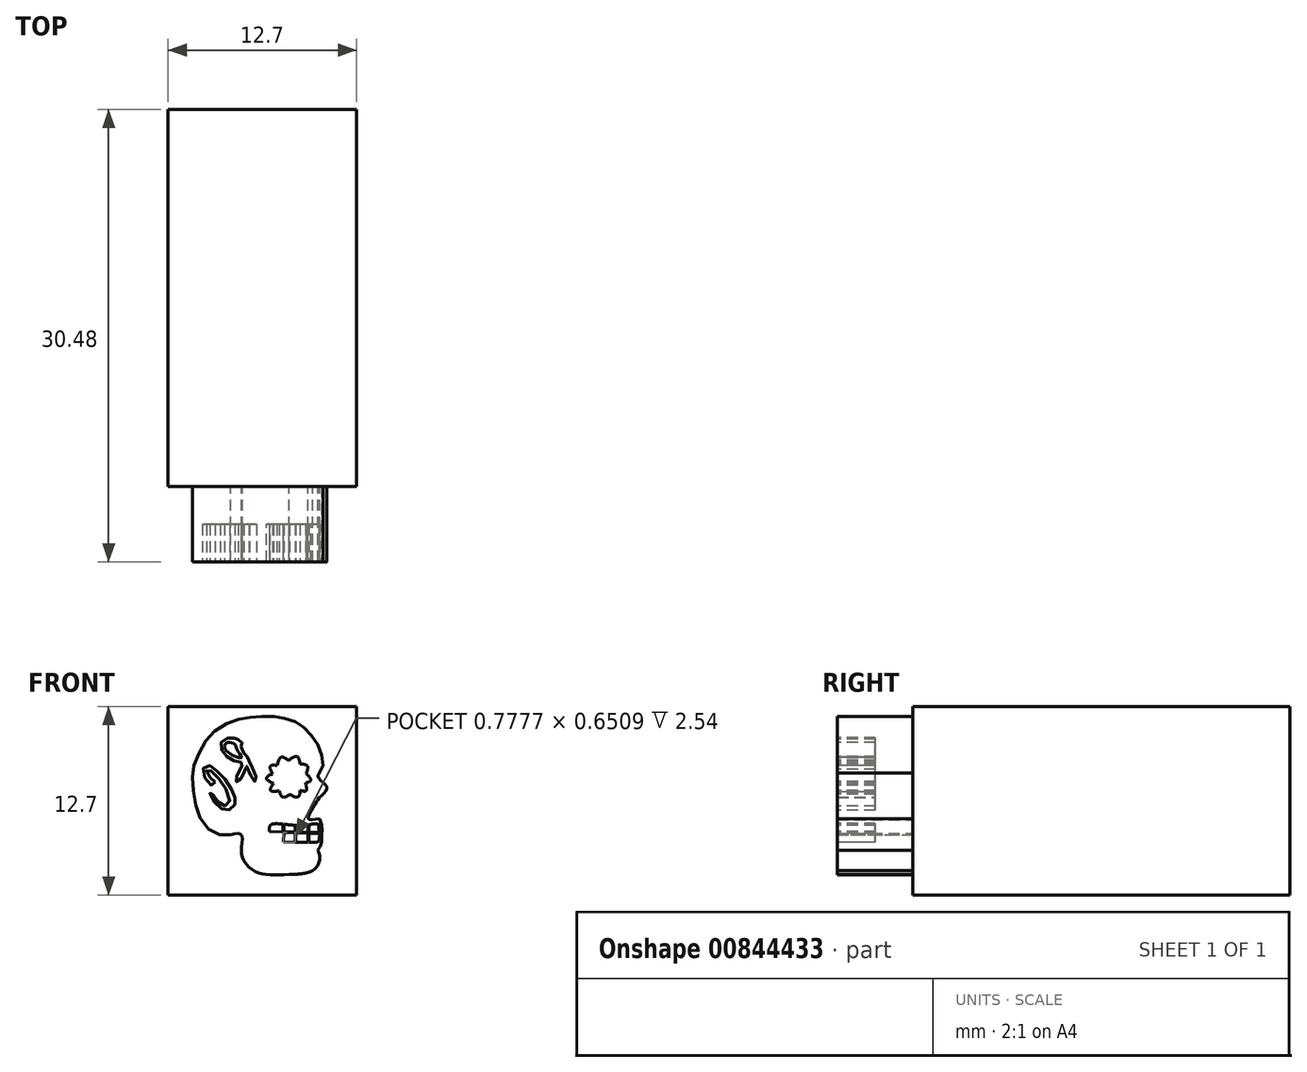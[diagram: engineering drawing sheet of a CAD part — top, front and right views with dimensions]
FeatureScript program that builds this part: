
annotation { "Feature Type Name" : "Feature", "Feature Type Description" : "" }
export const myFeature = defineFeature(function(context is Context, id is Id, definition is map)
    precondition{}
    {
        {
            var Q0;
            Q0=qCreatedBy(makeId("Front.planeOp"),FACE);
            var sketch = newSketch(context, id + "F0", { "sketchPlane" : qUnion([Q0])});
            skArc(sketch, "E0", {"start": v(-2.96, 1.65) * mm, "mid": v(-2.52, 2.28) * mm, "end": v(-2.62, 3.03) * mm});
            skFitSpline(sketch, "E1", {"points": [v(-4.55, 1.4) * mm, v(-2.96, 1.65) * mm], "startDerivative": vector(1.7, 0) * mm, "endDerivative": vector(1.51, 0.7) * mm});
            skFitSpline(sketch, "E2", {"points": [v(-2.49, 5.13) * mm, v(-2.35, 4.58) * mm, v(-2.35, 4.15) * mm, v(-2.35, 3.77) * mm, v(-2.62, 3.03) * mm], "startDerivative": vector(1.13, -2.5) * mm, "endDerivative": vector(-2.25, -2.73) * mm});
            skFitSpline(sketch, "E3", {"points": [v(-8.49, 4.08) * mm, v(-9.32, 4.08) * mm, v(-10.36, 4.88) * mm, v(-10.86, 6.14) * mm, v(-11.05, 7.58) * mm, v(-10.98, 8.64) * mm, v(-10.5, 9.83) * mm, v(-9.7, 10.94) * mm, v(-8.49, 11.66) * mm, v(-7.5, 11.93) * mm, v(-6.53, 12.03) * mm, v(-5.49, 12.02) * mm, v(-4.7, 11.87) * mm, v(-3.86, 11.55) * mm, v(-3.27, 11.01) * mm, v(-2.68, 10.28) * mm, v(-2.36, 9.45) * mm, v(-2.28, 8.68) * mm, v(-2.5, 8.22) * mm], "startDerivative": vector(-16.18, -2.66) * mm, "endDerivative": vector(-3.8, -12.82) * mm});
            skFitSpline(sketch, "E4", {"points": [v(-2.49, 5.13) * mm, v(-3.25, 5.13) * mm, v(-2.88, 5.99) * mm, v(-2.49, 6.59) * mm, v(-2, 7.19) * mm, v(-2.35, 7.65) * mm, v(-2.5, 8.22) * mm], "startDerivative": vector(-6.38, 0.02) * mm, "endDerivative": vector(4.2, 4.48) * mm});
            skFitSpline(sketch, "E5", {"points": [v(-8.49, 4.08) * mm, v(-7.77, 4.08) * mm, v(-7.74, 3.33) * mm, v(-7.65, 2.44) * mm, v(-6.94, 1.64) * mm, v(-6.06, 1.39) * mm, v(-4.55, 1.4) * mm], "startDerivative": vector(6.23, 1.32) * mm, "endDerivative": vector(7.7, 0.3) * mm});
            skSolve(sketch);
        }
        {
            var Q0;
            Q0=qCreatedBy(makeId("Front.planeOp"),FACE);
            var sketch = newSketch(context, id + "F1", { "sketchPlane" : qUnion([Q0])});
            skLineSegment(sketch, "E6.bottom", {"start": v(0, 0) * mm, "end": v(-12.7, 0) * mm});
            skLineSegment(sketch, "E6.top", {"start": v(0, 12.7) * mm, "end": v(-12.7, 12.7) * mm});
            skLineSegment(sketch, "E6.left", {"start": v(0, 0) * mm, "end": v(0, 12.7) * mm});
            skLineSegment(sketch, "E6.right", {"start": v(-12.7, 0) * mm, "end": v(-12.7, 12.7) * mm});
            skSolve(sketch);
        }
        {
            var Q0;
            Q0=qSketchRegion(id+"F0",true);
            extrude(context, id + "F2", {"entities" : qUnion([Q0]), "depth" : 5.08 * mm, "offsetDistance" : 25.4 * mm});
        }
        {
            var Q0;
            Q0=makeQuery(id+"F2.opExtrude","CAP_FACE",FACE,{"disambiguationData":[OSD([sQuery(id+"F0.wireOp",EDGE,"E0"),sQuery(id+"F0.wireOp",EDGE,"E1"),sQuery(id+"F0.wireOp",EDGE,"E2"),sQuery(id+"F0.wireOp",EDGE,"E3"),sQuery(id+"F0.wireOp",EDGE,"E4"),sQuery(id+"F0.wireOp",EDGE,"E5")])],"isStart":false});
            var sketch = newSketch(context, id + "F3", { "sketchPlane" : qUnion([Q0])});
            skFitSpline(sketch, "E7", {"points": [v(-5.37, 8.72) * mm, v(-5.09, 9.3) * mm, v(-4.59, 9.09) * mm], "startDerivative": vector(0.47, 1.45) * mm, "endDerivative": vector(1.15, -0.78) * mm});
            skFitSpline(sketch, "E8", {"points": [v(-4.59, 9.09) * mm, v(-4, 9.34) * mm, v(-3.8, 8.84) * mm], "startDerivative": vector(1.32, 0.85) * mm, "endDerivative": vector(0.23, -1.41) * mm});
            skFitSpline(sketch, "E9", {"points": [v(-3.8, 8.84) * mm, v(-3.33, 8.7) * mm, v(-3.4, 8.2) * mm], "startDerivative": vector(1.47, -0.06) * mm, "endDerivative": vector(-0.68, -1.2) * mm});
            skFitSpline(sketch, "E10", {"points": [v(-3.4, 8.2) * mm, v(-3.09, 7.74) * mm, v(-3.45, 7.56) * mm], "startDerivative": vector(0.96, -0.98) * mm, "endDerivative": vector(-1.07, -0.3) * mm});
            skFitSpline(sketch, "E11", {"points": [v(-3.45, 7.56) * mm, v(-3.4, 7.03) * mm, v(-3.8, 7.05) * mm], "startDerivative": vector(0.3, -1.24) * mm, "endDerivative": vector(-1.07, 0.2) * mm});
            skFitSpline(sketch, "E12", {"points": [v(-3.8, 7.05) * mm, v(-3.96, 6.61) * mm, v(-4.5, 6.8) * mm], "startDerivative": vector(-0.06, -1.45) * mm, "endDerivative": vector(-1.31, 0.89) * mm});
            skFitSpline(sketch, "E13", {"points": [v(-4.5, 6.8) * mm, v(-4.97, 6.6) * mm, v(-5.2, 7.02) * mm], "startDerivative": vector(-1.11, -0.95) * mm, "endDerivative": vector(-0.36, 1.4) * mm});
            skFitSpline(sketch, "E14", {"points": [v(-5.2, 7.02) * mm, v(-5.8, 7.05) * mm, v(-5.6, 7.52) * mm], "startDerivative": vector(-1.8, -0.17) * mm, "endDerivative": vector(1.04, 1.25) * mm});
            skFitSpline(sketch, "E15", {"points": [v(-5.6, 7.52) * mm, v(-6.08, 7.87) * mm, v(-5.65, 8.17) * mm], "startDerivative": vector(-1.95, 0.8) * mm, "endDerivative": vector(1.88, 0.54) * mm});
            skFitSpline(sketch, "E16", {"points": [v(-5.65, 8.17) * mm, v(-5.82, 8.67) * mm, v(-5.37, 8.72) * mm], "startDerivative": vector(-1.13, 1.61) * mm, "endDerivative": vector(1.77, -0.5) * mm});
            skFitSpline(sketch, "E17", {"points": [v(-2.58, 4.77) * mm, v(-3.23, 4.74) * mm, v(-4.58, 4.74) * mm, v(-5.8, 4.73) * mm, v(-5.9, 4.23) * mm, v(-5.82, 3.73) * mm, v(-5, 3.58) * mm, v(-3.89, 3.56) * mm, v(-2.84, 3.54) * mm, v(-2.58, 3.63) * mm, v(-2.5, 4.16) * mm, v(-2.54, 4.47) * mm, v(-2.58, 4.77) * mm]});
            skLineSegment(sketch, "E18", {"start": v(-5.9, 4.28) * mm, "end": v(-2.51, 4.22) * mm});
            skLineSegment(sketch, "E19", {"start": v(-5.9, 4.23) * mm, "end": v(-2.5, 4.16) * mm});
            skLineSegment(sketch, "E20", {"start": v(-4.96, 4.78) * mm, "end": v(-4.99, 3.58) * mm});
            skLineSegment(sketch, "E21", {"start": v(-4.99, 3.58) * mm, "end": v(-5, 3.58) * mm});
            skLineSegment(sketch, "E22", {"start": v(-4.9, 4.78) * mm, "end": v(-4.92, 3.58) * mm});
            skLineSegment(sketch, "E23", {"start": v(-4.15, 4.7) * mm, "end": v(-4.15, 3.56) * mm});
            skLineSegment(sketch, "E24", {"start": v(-3.23, 4.74) * mm, "end": v(-3.23, 3.55) * mm});
            skLineSegment(sketch, "E25", {"start": v(-3.28, 4.73) * mm, "end": v(-3.28, 3.55) * mm});
            skLineSegment(sketch, "E26", {"start": v(-4.11, 4.7) * mm, "end": v(-4.11, 3.56) * mm});
            skSolve(sketch);
        }
        {
            var Q0;
            Q0=makeQuery(id+"F3.imprint","IMPRINT",FACE,{"disambiguationData":[TD([[makeQuery(id+"F3.imprint","IMPRINT",EDGE,{"derivedFrom":sQuery(id+"F3.wireOp",EDGE,"E7")}),-1.0]])]});
            var Q1;
            {var subQ0=sQuery(id+"F3.wireOp",EDGE,"E18");var subQ1=sQuery(id+"F3.wireOp",EDGE,"E17");var subQ2=makeQuery(id+"F3.imprint","INTERSECT",VERTEX,{"disambiguationData":[OD(0.0)],"derivedFrom":[subQ1,subQ0]});Q1=makeQuery(id+"F3.imprint","IMPRINT",FACE,{"disambiguationData":[TD([[makeQuery(id+"F3.imprint","IMPRINT",EDGE,{"disambiguationData":[TD([[subQ2,1.0]])],"derivedFrom":subQ1}),1.0]])]});}
            var Q2;
            {var subQ0=sQuery(id+"F3.wireOp",EDGE,"E22");var subQ1=sQuery(id+"F3.wireOp",EDGE,"E17");var subQ2=makeQuery(id+"F3.imprint","INTERSECT",VERTEX,{"disambiguationData":[OD(0.0)],"derivedFrom":[subQ1,subQ0]});Q2=makeQuery(id+"F3.imprint","IMPRINT",FACE,{"disambiguationData":[TD([[makeQuery(id+"F3.imprint","IMPRINT",EDGE,{"disambiguationData":[TD([[subQ2,1.0]])],"derivedFrom":subQ1}),1.0]])]});}
            var Q3;
            {var subQ0=sQuery(id+"F3.wireOp",EDGE,"nEHl1WmI-M9KE-TG4T-uo55-SjTNBp4atS7q");var subQ1=sQuery(id+"F3.wireOp",EDGE,"E17");var subQ2=makeQuery(id+"F3.imprint","INTERSECT",VERTEX,{"derivedFrom":[subQ1,subQ0]});Q3=makeQuery(id+"F3.imprint","IMPRINT",FACE,{"disambiguationData":[TD([[makeQuery(id+"F3.imprint","IMPRINT",EDGE,{"disambiguationData":[TD([[subQ2,1.0]])],"derivedFrom":subQ1}),1.0]])]});}
            var Q4;
            {var subQ0=sQuery(id+"F3.wireOp",EDGE,"E18");var subQ1=sQuery(id+"F3.wireOp",EDGE,"E17");var subQ2=makeQuery(id+"F3.imprint","INTERSECT",VERTEX,{"disambiguationData":[OD(1.0)],"derivedFrom":[subQ1,subQ0]});Q4=makeQuery(id+"F3.imprint","IMPRINT",FACE,{"disambiguationData":[TD([[makeQuery(id+"F3.imprint","IMPRINT",EDGE,{"disambiguationData":[TD([[subQ2,-1.0]])],"derivedFrom":subQ1}),1.0]])]});}
            var Q5;
            {var subQ0=sQuery(id+"F3.wireOp",EDGE,"E19");var subQ1=sQuery(id+"F3.wireOp",EDGE,"E17");var subQ2=makeQuery(id+"F3.imprint","INTERSECT",VERTEX,{"disambiguationData":[OD(1.0)],"derivedFrom":[subQ1,subQ0]});Q5=makeQuery(id+"F3.imprint","IMPRINT",FACE,{"disambiguationData":[TD([[makeQuery(id+"F3.imprint","IMPRINT",EDGE,{"disambiguationData":[TD([[subQ2,1.0]])],"derivedFrom":subQ1}),1.0]])]});}
            var Q6;
            {var subQ1=sQuery(id+"F3.wireOp",EDGE,"E17");var subQ3=makeQuery(id+"F3.imprint","IMPRINT",VERTEX,{"derivedFrom":subQ1});Q6=makeQuery(id+"F3.imprint","IMPRINT",FACE,{"disambiguationData":[TD([[makeQuery(id+"F3.imprint","IMPRINT",EDGE,{"disambiguationData":[TD([[subQ3,1.0]])],"derivedFrom":subQ1}),1.0]])]});}
            var Q7;
            {var subQ0=sQuery(id+"F3.wireOp",EDGE,"E22");var subQ1=sQuery(id+"F3.wireOp",EDGE,"E17");var subQ2=makeQuery(id+"F3.imprint","INTERSECT",VERTEX,{"disambiguationData":[OD(1.0)],"derivedFrom":[subQ1,subQ0]});Q7=makeQuery(id+"F3.imprint","IMPRINT",FACE,{"disambiguationData":[TD([[makeQuery(id+"F3.imprint","IMPRINT",EDGE,{"disambiguationData":[TD([[subQ2,-1.0]])],"derivedFrom":subQ1}),1.0]])]});}
            var Q8;
            {var subQ0=sQuery(id+"F3.wireOp",EDGE,"E25");var subQ1=sQuery(id+"F3.wireOp",EDGE,"E17");var subQ2=makeQuery(id+"F3.imprint","INTERSECT",VERTEX,{"disambiguationData":[OD(1.0)],"derivedFrom":[subQ1,subQ0]});Q8=makeQuery(id+"F3.imprint","IMPRINT",FACE,{"disambiguationData":[TD([[makeQuery(id+"F3.imprint","IMPRINT",EDGE,{"disambiguationData":[TD([[subQ2,1.0]])],"derivedFrom":subQ1}),1.0]])]});}
            var Q9;
            {var subQ0=sQuery(id+"F3.wireOp",EDGE,"E25");var subQ1=sQuery(id+"F3.wireOp",EDGE,"E17");var subQ2=makeQuery(id+"F3.imprint","INTERSECT",VERTEX,{"disambiguationData":[OD(0.0)],"derivedFrom":[subQ1,subQ0]});Q9=makeQuery(id+"F3.imprint","IMPRINT",FACE,{"disambiguationData":[TD([[makeQuery(id+"F3.imprint","IMPRINT",EDGE,{"disambiguationData":[TD([[subQ2,-1.0]])],"derivedFrom":subQ1}),1.0]])]});}
            extrude(context, id + "F4", {"entities" : qUnion([Q0, Q1, Q2, Q3, Q4, Q5, Q6, Q7, Q8, Q9]), "operationType" : NewBodyOperationType.REMOVE, "oppositeDirection" : true, "depth" : 2.54 * mm, "offsetDistance" : 25.4 * mm});
        }
        {
            var Q0;
            Q0=qSketchRegion(id+"F1",true);
            extrude(context, id + "F5", {"entities" : qUnion([Q0]), "operationType" : NewBodyOperationType.ADD, "oppositeDirection" : true, "depth" : 25.4 * mm, "offsetDistance" : 25.4 * mm});
        }
        {
            var Q0;
            Q0=makeQuery(id+"F2.opExtrude","CAP_FACE",FACE,{"disambiguationData":[OSD([sQuery(id+"F0.wireOp",EDGE,"E0"),sQuery(id+"F0.wireOp",EDGE,"E1"),sQuery(id+"F0.wireOp",EDGE,"E2"),sQuery(id+"F0.wireOp",EDGE,"E3"),sQuery(id+"F0.wireOp",EDGE,"E4"),sQuery(id+"F0.wireOp",EDGE,"E5")])],"isStart":false});
            var sketch = newSketch(context, id + "F6", { "sketchPlane" : qUnion([Q0])});
            skFitSpline(sketch, "E27", {"points": [v(-7.8, 10) * mm, v(-7.7, 9.77) * mm, v(-7.57, 9.5) * mm, v(-7.46, 9.29) * mm, v(-7.42, 9.34) * mm, v(-7.3, 9.3) * mm, v(-7.22, 9.19) * mm, v(-7.24, 9) * mm, v(-7.13, 8.78) * mm, v(-6.9, 8.28) * mm, v(-6.76, 7.9) * mm, v(-6.74, 7.74) * mm, v(-6.84, 7.66) * mm, v(-6.98, 7.68) * mm, v(-7.1, 8) * mm, v(-7.38, 8.6) * mm, v(-7.42, 8.72) * mm, v(-7.52, 8.47) * mm, v(-7.64, 8.12) * mm, v(-7.8, 7.82) * mm, v(-7.9, 7.66) * mm, v(-8.05, 7.63) * mm, v(-8.2, 7.76) * mm, v(-8.1, 8) * mm, v(-7.88, 8.44) * mm, v(-7.6, 8.96) * mm, v(-7.72, 8.96) * mm, v(-7.98, 8.98) * mm, v(-8.24, 9.03) * mm, v(-8.57, 9.2) * mm, v(-8.82, 9.42) * mm, v(-9.05, 9.7) * mm, v(-9.16, 9.93) * mm, v(-9.14, 10.27) * mm, v(-8.87, 10.54) * mm, v(-8.62, 10.58) * mm, v(-8.29, 10.52) * mm, v(-8.21, 10.61) * mm, v(-8.08, 10.58) * mm, v(-8, 10.5) * mm, v(-7.99, 10.41) * mm, v(-7.84, 10.35) * mm, v(-7.67, 10.2) * mm, v(-7.65, 10.05) * mm, v(-7.8, 10) * mm]});
            skFitSpline(sketch, "E28", {"points": [v(-8.2, 10.18) * mm, v(-8.09, 9.9) * mm, v(-7.91, 9.57) * mm, v(-7.76, 9.28) * mm, v(-8.16, 9.32) * mm, v(-8.53, 9.55) * mm, v(-8.83, 9.8) * mm, v(-8.87, 10.13) * mm, v(-8.7, 10.29) * mm, v(-8.42, 10.27) * mm, v(-8.2, 10.18) * mm]});
            skFitSpline(sketch, "E29", {"points": [v(-9.55, 7.61) * mm, v(-9.55, 7.45) * mm, v(-9.69, 7.39) * mm, v(-9.95, 7.51) * mm, v(-10.22, 7.9) * mm, v(-10.37, 8.3) * mm, v(-10.28, 8.64) * mm, v(-10.02, 8.76) * mm, v(-9.79, 8.68) * mm, v(-9.5, 8.43) * mm, v(-9.15, 8.1) * mm, v(-8.76, 7.66) * mm, v(-8.41, 7.09) * mm, v(-8.3, 6.8) * mm, v(-8.2, 6.46) * mm, v(-8.2, 6.21) * mm, v(-8.2, 6.14) * mm, v(-8.39, 5.83) * mm, v(-8.54, 5.75) * mm, v(-8.76, 5.71) * mm, v(-9.06, 5.8) * mm, v(-9.4, 6.06) * mm, v(-9.67, 6.37) * mm, v(-9.9, 6.78) * mm, v(-9.84, 6.9) * mm, v(-9.75, 6.87) * mm, v(-9.65, 6.73) * mm, v(-9.5, 6.52) * mm, v(-9.36, 6.32) * mm, v(-9.14, 6.14) * mm, v(-8.88, 6.01) * mm, v(-8.63, 6.06) * mm, v(-8.55, 6.4) * mm, v(-8.75, 7.01) * mm, v(-9.13, 7.65) * mm, v(-9.47, 8.08) * mm, v(-9.8, 8.38) * mm, v(-9.97, 8.47) * mm, v(-10.06, 8.45) * mm, v(-10.1, 8.35) * mm, v(-10.02, 8.15) * mm, v(-9.85, 7.9) * mm, v(-9.72, 7.73) * mm, v(-9.55, 7.61) * mm]});
            skSolve(sketch);
        }
        {
            var Q0;
            Q0 = qSketchRegion(id + "F6", true);
            extrude(context, id + "F7", {"entities" : qUnion([Q0]), "operationType" : NewBodyOperationType.REMOVE, "oppositeDirection" : true, "depth" : 2.54 * mm, "offsetDistance" : 25.4 * mm});
        }
    });
